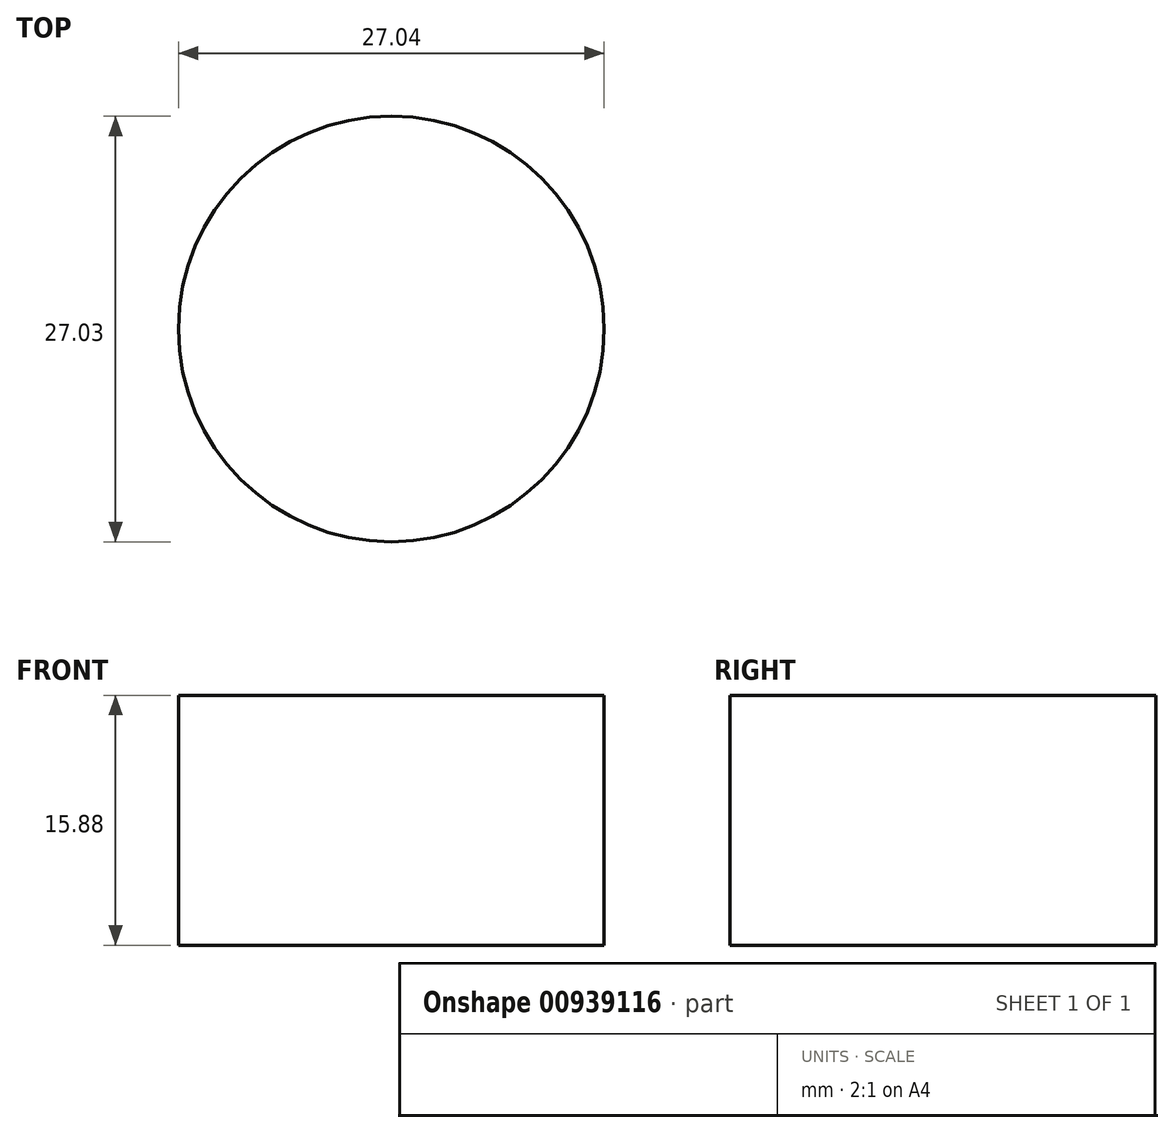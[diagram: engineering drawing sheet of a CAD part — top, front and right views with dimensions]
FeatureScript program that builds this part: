
annotation { "Feature Type Name" : "Feature", "Feature Type Description" : "" }
export const myFeature = defineFeature(function(context is Context, id is Id, definition is map)
    precondition{}
    {
        {
            var Q0;
            Q0=qCreatedBy(makeId("Top.planeOp"),FACE);
            var sketch = newSketch(context, id + "F0", { "sketchPlane" : qUnion([Q0])});
            skCircle(sketch, "E0", {"center": v(-36.9, 43.92) * mm, "radius": 13.52 * mm});
            skSolve(sketch);
        }
        {
            var Q0;
            Q0=makeQuery(id+"F0.imprint","IMPRINT",FACE,{"disambiguationData":[TD([[makeQuery(id+"F0.imprint","IMPRINT",EDGE,{"derivedFrom":sQuery(id+"F0.wireOp",EDGE,"E0")}),1.0]])]});
            extrude(context, id + "F1", {"entities" : qUnion([Q0]), "oppositeDirection" : true, "depth" : 15.88 * mm, "offsetDistance" : 25.4 * mm, "hasDraft" : true, "draftAngle" : 0 * degree});
        }
    });
